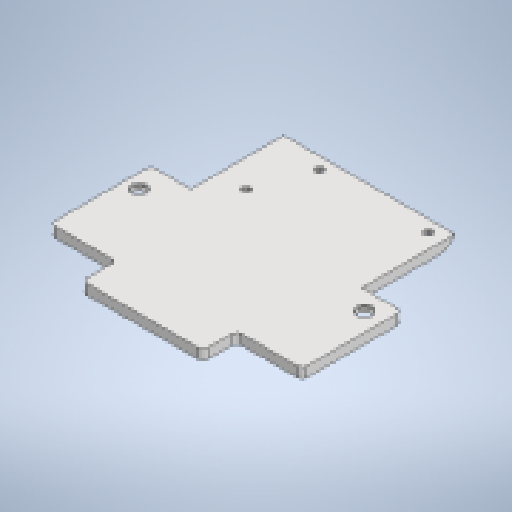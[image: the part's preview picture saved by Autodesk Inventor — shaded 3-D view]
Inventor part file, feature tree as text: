
AUTODESK INVENTOR PART (.ipt)
format: ipt  version: 2023.5 (Build 275446000, 446)  size: 280,576 bytes
history: native  units: mm
features: reference x14, sketch x10, extrude x8, other x6, fillet x4, hole x3, chamfer x2, projected_geometry x2
ambient origin geometry x8: Origin, YZ Plane, XZ Plane, XY Plane, X Axis, Y Axis, Z Axis, Center Point
bodies: Body1 (feature_tree)
feature tree (49):
  other  "Bryła1"
  extrude  "Wyciągnięcie proste1"  Depth=50.0mm
  extrude  "Wyciągnięcie proste3"  Depth=50.0mm
  extrude  "Wyciągnięcie proste5"  Depth=8.0mm
  extrude  "Wyciągnięcie proste6"  Depth=20.0mm
  fillet  "Zaokrąglenie1"  Radius=8.0mm
  extrude  "Wyciągnięcie proste8"  Depth=20.0mm
  extrude  "Wyciągnięcie proste9"  Depth=2.0mm TaperAngle=0.0deg
  sketch  "Szkic11"
  hole  "Otwór1"  [1 undecoded]
  hole  "Otwór2"  [1 undecoded]
  extrude  "Wyciągnięcie proste10"  Depth=8.0mm
  fillet  "Zaokrąglenie2"  Radius=8.0mm
  extrude  "Wyciągnięcie proste11"  TaperAngle=0.0deg  [1 undecoded]
  fillet  "Zaokrąglenie3"  Radius=1.0mm
  fillet  "Zaokrąglenie4"  Radius=10.0mm
  chamfer  "Faza1"  Distance=3.1mm
  hole  "Otwór3"  [1 undecoded]
  chamfer  "Faza2"  [1 undecoded]
  sketch  "Szkic1"
  sketch  "Szkic4"
  reference  "Odniesienie4"
  reference  "Odniesienie5"
  reference  "Odniesienie6"
  reference  "Odniesienie7"
  sketch  "Szkic6"
  projected_geometry  "Pętla rzutowana2"
  reference  "Odniesienie9"
  sketch  "Szkic7"
  projected_geometry  "Pętla rzutowana3"
  reference  "Odniesienie10"
  reference  "Odniesienie11"
  sketch  "Szkic9"
  sketch  "Szkic10"
  reference  "Odniesienie14"
  reference  "Odniesienie15"
  reference  "Odniesienie16"
  reference  "Odniesienie17"
  reference  "Odniesienie18"
  reference  "Odniesienie19"
  sketch  "Szkic12"
  sketch  "Szkic13"
  sketch  "Szkic14"
  reference  "Odniesienie20"
  parser-record x1  (decoder bookkeeping rows leaked as tree rows — omitted from the tree; the rows remain in map.json)
  other  "stratos_v2_mechanics.iam"
  other  "montaz_osi:1"
  other  "nozzyk:1"
  other  "scianka_prawa:1"
note: 5 required parameter values undecoded (feature->parameter linkage not recoverable at this tier; creation-order binding heuristic only, values carry confidence <= 0.55)
note: 1 file-system path scrubbed to <path> (originals preserved in map.json)
